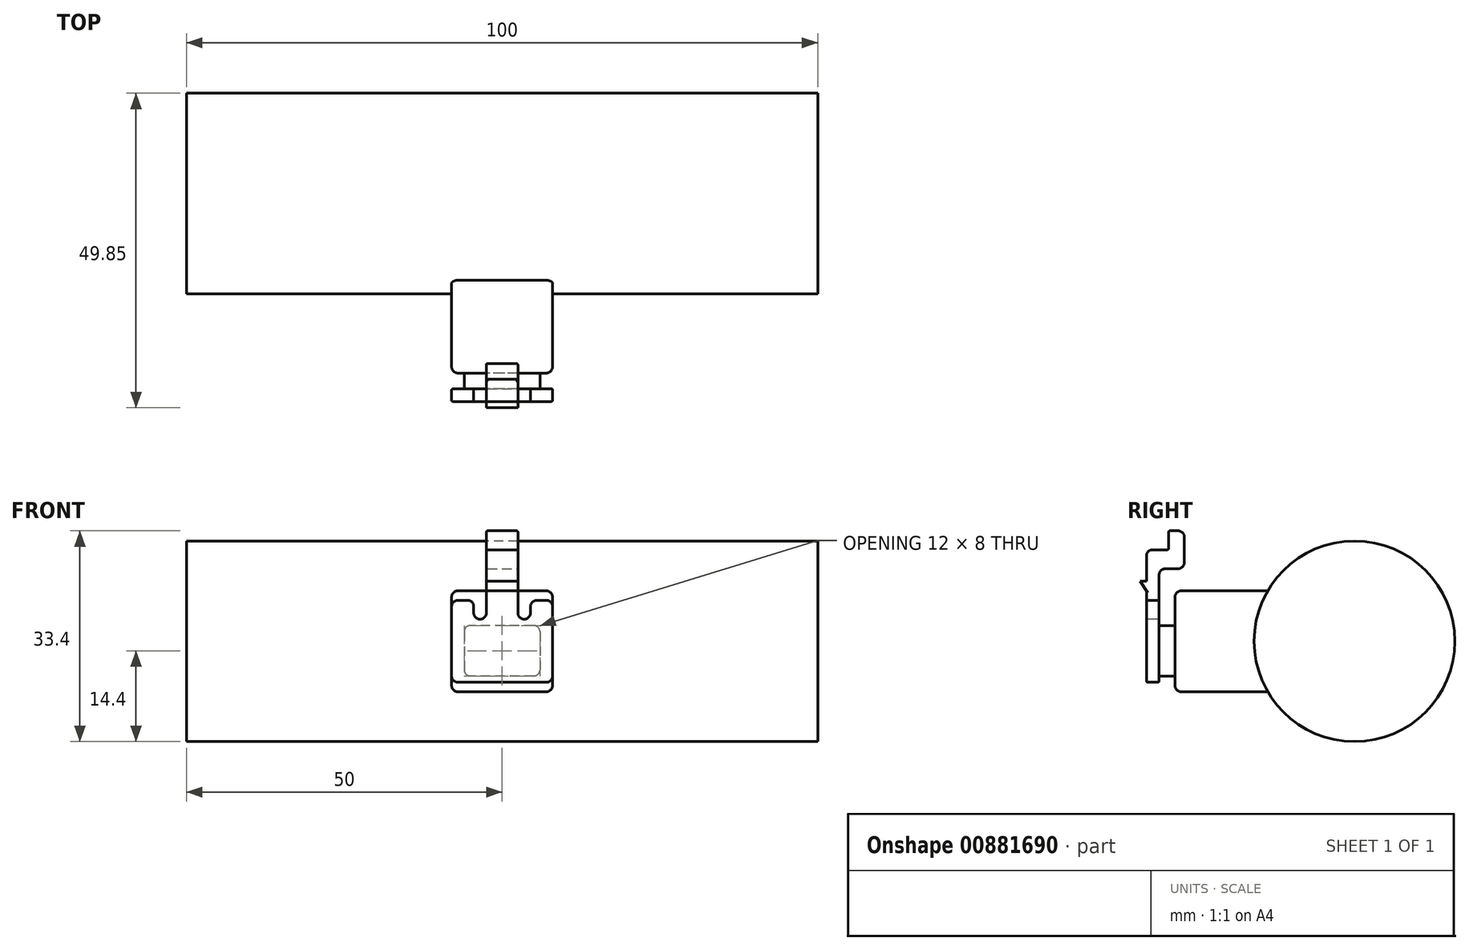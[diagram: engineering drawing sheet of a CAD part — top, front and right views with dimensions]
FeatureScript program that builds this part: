
annotation { "Feature Type Name" : "Feature", "Feature Type Description" : "" }
export const myFeature = defineFeature(function(context is Context, id is Id, definition is map)
    precondition{}
    {
        {
            var Q0;
            Q0=qCreatedBy(makeId("Front.planeOp"),FACE);
            var sketch = newSketch(context, id + "F0", { "sketchPlane" : qUnion([Q0])});
            skLineSegment(sketch, "E0.bottom", {"start": v(8, -5) * mm, "end": v(-8, -5) * mm});
            skLineSegment(sketch, "E0.top", {"start": v(8, 5) * mm, "end": v(-8, 5) * mm});
            skLineSegment(sketch, "E0.left", {"start": v(8, -5) * mm, "end": v(8, 5) * mm});
            skLineSegment(sketch, "E0.right", {"start": v(-8, -5) * mm, "end": v(-8, 5) * mm});
            skPoint(sketch, "E0.middle", {"position": v(0, 0) * mm});
            skPoint(sketch, "E1", {"position": v(0, 5) * mm});
            skLineSegment(sketch, "E2.bottom", {"start": v(-2.5, 13) * mm, "end": v(2.5, 13) * mm});
            skLineSegment(sketch, "E2.top", {"start": v(-2.5, 5) * mm, "end": v(2.5, 5) * mm});
            skLineSegment(sketch, "E2.left", {"start": v(-2.5, 13) * mm, "end": v(-2.5, 5) * mm});
            skLineSegment(sketch, "E2.right", {"start": v(2.5, 13) * mm, "end": v(2.5, 5) * mm});
            skLineSegment(sketch, "E3.bottom", {"start": v(-8, 8) * mm, "end": v(-4.5, 8) * mm});
            skLineSegment(sketch, "E3.top", {"start": v(-8, 5) * mm, "end": v(-4.5, 5) * mm});
            skLineSegment(sketch, "E3.left", {"start": v(-8, 8) * mm, "end": v(-8, 5) * mm});
            skLineSegment(sketch, "E3.right", {"start": v(-4.5, 8) * mm, "end": v(-4.5, 5) * mm});
            skLineSegment(sketch, "E4.bottom", {"start": v(4.5, 8) * mm, "end": v(8, 8) * mm});
            skLineSegment(sketch, "E4.top", {"start": v(4.5, 5) * mm, "end": v(8, 5) * mm});
            skLineSegment(sketch, "E4.left", {"start": v(4.5, 8) * mm, "end": v(4.5, 5) * mm});
            skLineSegment(sketch, "E4.right", {"start": v(8, 8) * mm, "end": v(8, 5) * mm});
            skLineSegment(sketch, "E5.top", {"start": v(-2.5, 16) * mm, "end": v(2.5, 16) * mm});
            skLineSegment(sketch, "E5.left", {"start": v(-2.5, 13) * mm, "end": v(-2.5, 16) * mm});
            skLineSegment(sketch, "E5.right", {"start": v(2.5, 13) * mm, "end": v(2.5, 16) * mm});
            skPoint(sketch, "E6.visualSharp", {"position": v(-8, -5) * mm});
            skLineSegment(sketch, "E6.filletArc", {"start": v(-8, -5) * mm, "end": v(-8, -5) * mm});
            skPoint(sketch, "E7.visualSharp", {"position": v(8, -5) * mm});
            skLineSegment(sketch, "E7.filletArc", {"start": v(8, -5) * mm, "end": v(8, -5) * mm});
            skPoint(sketch, "E8.visualSharp", {"position": v(8, 8) * mm});
            skLineSegment(sketch, "E8.filletArc", {"start": v(8, 8) * mm, "end": v(8, 8) * mm});
            skPoint(sketch, "E9.visualSharp", {"position": v(4.5, 8) * mm});
            skLineSegment(sketch, "E9.filletArc", {"start": v(4.5, 8) * mm, "end": v(4.5, 8) * mm});
            skPoint(sketch, "E10.visualSharp", {"position": v(-4.5, 8) * mm});
            skLineSegment(sketch, "E10.filletArc", {"start": v(-4.5, 8) * mm, "end": v(-4.5, 8) * mm});
            skPoint(sketch, "E11.visualSharp", {"position": v(-8, 8) * mm});
            skLineSegment(sketch, "E11.filletArc", {"start": v(-8, 8) * mm, "end": v(-8, 8) * mm});
            skLineSegment(sketch, "E12.bottom", {"start": v(2.5, 11) * mm, "end": v(-2.5, 11) * mm});
            skLineSegment(sketch, "E12.top", {"start": v(2.5, 9.5) * mm, "end": v(-2.5, 9.5) * mm});
            skLineSegment(sketch, "E12.left", {"start": v(2.5, 11) * mm, "end": v(2.5, 9.5) * mm});
            skLineSegment(sketch, "E12.right", {"start": v(-2.5, 11) * mm, "end": v(-2.5, 9.5) * mm});
            skPoint(sketch, "E13", {"position": v(0, 9.5) * mm});
            skSolve(sketch);
        }
        {
            var Q0;
            {var subQ0=sQuery(id+"F0.wireOp",EDGE,"E2.bottom");var subQ1=makeQuery(id+"F0.imprint","IMPRINT",EDGE,{"derivedFrom":subQ0});var subQ4=sQuery(id+"F0.wireOp",EDGE,"E12.top");var subQ7=sQuery(id+"F0.wireOp",EDGE,"E12.bottom");var subQ12=makeQuery(id+"F0.imprint","IMPRINT",EDGE,{"derivedFrom":subQ7});var subQ13=makeQuery(id+"F0.imprint","IMPRINT",EDGE,{"derivedFrom":subQ4});Q0=qUnion([makeQuery(id+"F0.imprint","IMPRINT",FACE,{"disambiguationData":[TD([[subQ13,1.0]])]}),makeQuery(id+"F0.imprint","IMPRINT",FACE,{"disambiguationData":[TD([[makeQuery(id+"F0.imprint","IMPRINT",EDGE,{"derivedFrom":sQuery(id+"F0.wireOp",EDGE,"E0.bottom")}),-1.0]])]}),makeQuery(id+"F0.imprint","IMPRINT",FACE,{"disambiguationData":[TD([[makeQuery(id+"F0.imprint","IMPRINT",EDGE,{"derivedFrom":sQuery(id+"F0.wireOp",EDGE,"E4.bottom")}),-1.0]])]}),makeQuery(id+"F0.imprint","IMPRINT",FACE,{"disambiguationData":[TD([[subQ1,-1.0]])]}),makeQuery(id+"F0.imprint","IMPRINT",FACE,{"disambiguationData":[TD([[makeQuery(id+"F0.imprint","IMPRINT",EDGE,{"derivedFrom":sQuery(id+"F0.wireOp",EDGE,"E3.bottom")}),-1.0]])]}),makeQuery(id+"F0.imprint","IMPRINT",FACE,{"disambiguationData":[TD([[subQ12,1.0]])]}),makeQuery(id+"F0.imprint","IMPRINT",FACE,{"disambiguationData":[TD([[subQ1,1.0]])]})]);}
            extrude(context, id + "F1", {"entities" : qUnion([Q0]), "oppositeDirection" : true, "depth" : 2 * mm, "offsetDistance" : 25 * mm});
        }
        {
            var Q0;
            Q0=makeQuery(id+"F0.imprint","IMPRINT",FACE,{"disambiguationData":[TD([[makeQuery(id+"F0.imprint","IMPRINT",EDGE,{"derivedFrom":sQuery(id+"F0.wireOp",EDGE,"E2.bottom")}),1.0]])]});
            extrude(context, id + "F2", {"entities" : qUnion([Q0]), "operationType" : NewBodyOperationType.ADD, "oppositeDirection" : true, "depth" : 6 * mm, "offsetDistance" : 25 * mm, "hasSecondDirection" : true, "secondDirectionOppositeDirection" : true, "secondDirectionDepth" : 2 * mm});
        }
        {
            var Q0;
            {var subQ0=sQuery(id+"F0.wireOp",EDGE,"E5.top");Q0=makeQuery(id+"F2.boolean.opBoolean","MERGE",FACE,{"derivedFrom":[makeQuery(id+"F1.opExtrude","SWEPT_FACE",FACE,{"disambiguationData":[OSD([subQ0])]}),makeQuery(id+"F2.opExtrude","SWEPT_FACE",FACE,{"disambiguationData":[OSD([subQ0])]})]});}
            cPlane(context, id + "F3", {"entities" : qUnion([Q0]), "cplaneType" : CPlaneType.OFFSET, "offset" : 0 * mm, "width" : 150 * mm, "height" : 150 * mm});
        }
        {
            var Q0;
            Q0=qCreatedBy(id+"F3.planeOp",FACE);
            var sketch = newSketch(context, id + "F4", { "sketchPlane" : qUnion([Q0])});
            skPoint(sketch, "E14.0", {"position": v(2.5, 6) * mm});
            skPoint(sketch, "E15.0", {"position": v(-2.5, 6) * mm});
            skLineSegment(sketch, "E16.bottom", {"start": v(-2.5, 6) * mm, "end": v(2.5, 6) * mm});
            skLineSegment(sketch, "E16.top", {"start": v(-2.5, 3.5) * mm, "end": v(2.5, 3.5) * mm});
            skLineSegment(sketch, "E16.left", {"start": v(2.5, 6) * mm, "end": v(2.5, 3.5) * mm});
            skLineSegment(sketch, "E16.right", {"start": v(-2.5, 6) * mm, "end": v(-2.5, 3.5) * mm});
            skSolve(sketch);
        }
        {
            var Q0;
            Q0 = qSketchRegion(id + "F4", true);
            extrude(context, id + "F5", {"entities" : qUnion([Q0]), "operationType" : NewBodyOperationType.ADD, "depth" : 3 * mm, "offsetDistance" : 25 * mm});
        }
        {
            var Q0;
            {var subQ2=sQuery(id+"F0.wireOp",EDGE,"E12.bottom");Q0=makeQuery(id+"F0.imprint","IMPRINT",FACE,{"disambiguationData":[TD([[makeQuery(id+"F0.imprint","IMPRINT",EDGE,{"derivedFrom":subQ2}),1.0]])]});}
            extrude(context, id + "F6", {"entities" : qUnion([Q0]), "operationType" : NewBodyOperationType.ADD, "depth" : 1 * mm, "offsetDistance" : 25 * mm});
        }
        {
            var Q0;
            Q0=makeQuery(id+"F6.opExtrude","CAP_EDGE",EDGE,{"disambiguationData":[OSD([sQuery(id+"F0.wireOp",EDGE,"E12.top")])],"isStart":false});
            chamfer(context, id + "F7", {"entities" : qUnion([Q0]), "chamferType" : ChamferType.TWO_OFFSETS, "width1" : 1 * mm, "oppositeDirection" : false, "width2" : 1.5 * mm});
        }
        {
            var Q0;
            Q0=makeQuery(id+"F1.opExtrude","CAP_FACE",FACE,{"disambiguationData":[OSD([sQuery(id+"F0.wireOp",EDGE,"E0.bottom"),sQuery(id+"F0.wireOp",EDGE,"E0.top"),sQuery(id+"F0.wireOp",EDGE,"E0.left"),sQuery(id+"F0.wireOp",EDGE,"E0.right"),sQuery(id+"F0.wireOp",EDGE,"E2.left"),sQuery(id+"F0.wireOp",EDGE,"E2.right"),sQuery(id+"F0.wireOp",EDGE,"E3.bottom"),sQuery(id+"F0.wireOp",EDGE,"E3.left"),sQuery(id+"F0.wireOp",EDGE,"E3.right"),sQuery(id+"F0.wireOp",EDGE,"E4.bottom"),sQuery(id+"F0.wireOp",EDGE,"E4.left"),sQuery(id+"F0.wireOp",EDGE,"E4.right"),sQuery(id+"F0.wireOp",EDGE,"E5.top"),sQuery(id+"F0.wireOp",EDGE,"E5.left"),sQuery(id+"F0.wireOp",EDGE,"E5.right")])],"isStart":false});
            cPlane(context, id + "F8", {"entities" : qUnion([Q0]), "cplaneType" : CPlaneType.OFFSET, "offset" : 0 * mm, "width" : 150 * mm, "height" : 150 * mm});
        }
        {
            var Q0;
            Q0=qCreatedBy(id+"F8.planeOp",FACE);
            var sketch = newSketch(context, id + "F9", { "sketchPlane" : qUnion([Q0])});
            skLineSegment(sketch, "E17.bottom", {"start": v(-6, 4) * mm, "end": v(6, 4) * mm});
            skLineSegment(sketch, "E17.top", {"start": v(-6, -4) * mm, "end": v(6, -4) * mm});
            skLineSegment(sketch, "E17.left", {"start": v(-6, 4) * mm, "end": v(-6, -4) * mm});
            skLineSegment(sketch, "E17.right", {"start": v(6, 4) * mm, "end": v(6, -4) * mm});
            skPoint(sketch, "E18.0", {"position": v(8, 5) * mm});
            skPoint(sketch, "E19.0", {"position": v(-8, 5) * mm});
            skPoint(sketch, "E20.0", {"position": v(0, 5) * mm});
            skPoint(sketch, "E21", {"position": v(0, 4) * mm});
            skPoint(sketch, "E22.visualSharp", {"position": v(-6, 4) * mm});
            skLineSegment(sketch, "E22.filletArc", {"start": v(-6, 4) * mm, "end": v(-6, 4) * mm});
            skPoint(sketch, "E23.visualSharp", {"position": v(-6, -4) * mm});
            skLineSegment(sketch, "E23.filletArc", {"start": v(-6, -4) * mm, "end": v(-6, -4) * mm});
            skPoint(sketch, "E24.visualSharp", {"position": v(6, -4) * mm});
            skLineSegment(sketch, "E24.filletArc", {"start": v(6, -4) * mm, "end": v(6, -4) * mm});
            skPoint(sketch, "E25.visualSharp", {"position": v(6, 4) * mm});
            skLineSegment(sketch, "E25.filletArc", {"start": v(6, 4) * mm, "end": v(6, 4) * mm});
            skSolve(sketch);
        }
        {
            var Q0;
            Q0=makeQuery(id+"F9.imprint","IMPRINT",FACE,{"disambiguationData":[TD([[makeQuery(id+"F9.imprint","IMPRINT",EDGE,{"derivedFrom":sQuery(id+"F9.wireOp",EDGE,"E17.bottom")}),-1.0]])]});
            extrude(context, id + "F10", {"entities" : qUnion([Q0]), "operationType" : NewBodyOperationType.ADD, "depth" : 2.5 * mm, "offsetDistance" : 25 * mm});
        }
        {
            var Q0;
            Q0=makeQuery(id+"F10.opExtrude","CAP_FACE",FACE,{"disambiguationData":[OSD([sQuery(id+"F9.wireOp",EDGE,"E17.bottom"),sQuery(id+"F9.wireOp",EDGE,"E17.top"),sQuery(id+"F9.wireOp",EDGE,"E17.left"),sQuery(id+"F9.wireOp",EDGE,"E17.right")])],"isStart":false});
            cPlane(context, id + "F11", {"entities" : qUnion([Q0]), "cplaneType" : CPlaneType.OFFSET, "offset" : 0 * mm, "width" : 150 * mm, "height" : 150 * mm});
        }
        {
            var Q0;
            Q0=qCreatedBy(id+"F11.planeOp",FACE);
            var sketch = newSketch(context, id + "F12", { "sketchPlane" : qUnion([Q0])});
            skLineSegment(sketch, "E26.bottom", {"start": v(-8, 9.5) * mm, "end": v(8, 9.5) * mm});
            skLineSegment(sketch, "E26.top", {"start": v(-8, -6.5) * mm, "end": v(8, -6.5) * mm});
            skLineSegment(sketch, "E26.left", {"start": v(-8, 9.5) * mm, "end": v(-8, -6.5) * mm});
            skLineSegment(sketch, "E26.right", {"start": v(8, 9.5) * mm, "end": v(8, -6.5) * mm});
            skPoint(sketch, "E27", {"position": v(0, 9.5) * mm});
            skPoint(sketch, "E28", {"position": v(8, 1.5) * mm});
            skSolve(sketch);
        }
        {
            var Q0;
            Q0=makeQuery(id+"F12.imprint","IMPRINT",FACE,{"disambiguationData":[TD([[makeQuery(id+"F12.imprint","IMPRINT",EDGE,{"derivedFrom":sQuery(id+"F12.wireOp",EDGE,"E26.bottom")}),-1.0]])]});
            extrude(context, id + "F13", {"entities" : qUnion([Q0]), "operationType" : NewBodyOperationType.ADD, "depth" : 15 * mm, "offsetDistance" : 25 * mm});
        }
        {
            var Q0;
            Q0=qCreatedBy(makeId("Right.planeOp"),FACE);
            var sketch = newSketch(context, id + "F14", { "sketchPlane" : qUnion([Q0])});
            skCircle(sketch, "E29", {"center": v(32.95, 1.5) * mm, "radius": 15.9 * mm});
            skSolve(sketch);
        }
        {
            var Q0;
            Q0=makeQuery(id+"F14.imprint","IMPRINT",FACE,{"disambiguationData":[TD([[makeQuery(id+"F14.imprint","IMPRINT",EDGE,{"derivedFrom":sQuery(id+"F14.wireOp",EDGE,"E29")}),1.0]])]});
            extrude(context, id + "F15", {"entities" : qUnion([Q0]), "operationType" : NewBodyOperationType.REMOVE, "endBound" : BoundingType.SYMMETRIC, "depth" : 80 * mm, "offsetDistance" : 25 * mm});
        }
        {
            var Q0;
            Q0=makeQuery(id+"F2.boolean.opBoolean","INTERSECT",EDGE,{"derivedFrom":[makeQuery(id+"F1.opExtrude","CAP_FACE",FACE,{"disambiguationData":[OSD([sQuery(id+"F0.wireOp",EDGE,"E0.bottom"),sQuery(id+"F0.wireOp",EDGE,"E0.top"),sQuery(id+"F0.wireOp",EDGE,"E0.left"),sQuery(id+"F0.wireOp",EDGE,"E0.right"),sQuery(id+"F0.wireOp",EDGE,"E2.left"),sQuery(id+"F0.wireOp",EDGE,"E2.right"),sQuery(id+"F0.wireOp",EDGE,"E3.bottom"),sQuery(id+"F0.wireOp",EDGE,"E3.left"),sQuery(id+"F0.wireOp",EDGE,"E3.right"),sQuery(id+"F0.wireOp",EDGE,"E4.bottom"),sQuery(id+"F0.wireOp",EDGE,"E4.left"),sQuery(id+"F0.wireOp",EDGE,"E4.right"),sQuery(id+"F0.wireOp",EDGE,"E5.top"),sQuery(id+"F0.wireOp",EDGE,"E5.left"),sQuery(id+"F0.wireOp",EDGE,"E5.right"),sQuery(id+"F0.wireOp",EDGE,"E6.filletArc"),sQuery(id+"F0.wireOp",EDGE,"E7.filletArc"),sQuery(id+"F0.wireOp",EDGE,"E8.filletArc"),sQuery(id+"F0.wireOp",EDGE,"E9.filletArc"),sQuery(id+"F0.wireOp",EDGE,"E10.filletArc"),sQuery(id+"F0.wireOp",EDGE,"E11.filletArc")])],"isStart":false}),makeQuery(id+"F2.opExtrude","SWEPT_FACE",FACE,{"disambiguationData":[OSD([sQuery(id+"F0.wireOp",EDGE,"E2.bottom")])]})]});
            var Q1;
            Q1=makeQuery(id+"F2.opExtrude","CAP_EDGE",EDGE,{"disambiguationData":[OSD([sQuery(id+"F0.wireOp",EDGE,"E2.bottom")])],"isStart":false});
            var Q2;
            Q2=makeQuery(id+"F1.opExtrude","CAP_EDGE",EDGE,{"disambiguationData":[OSD([sQuery(id+"F0.wireOp",EDGE,"E5.top")])],"isStart":true});
            var Q3;
            Q3=makeQuery(id+"F5.opExtrude","CAP_EDGE",EDGE,{"disambiguationData":[OSD([sQuery(id+"F4.wireOp",EDGE,"E16.top")])],"isStart":true});
            var Q4;
            Q4=makeQuery(id+"F1.opExtrude","SWEPT_EDGE",EDGE,{"disambiguationData":[OSD([sQuery(id+"F0.wireOp",EDGE,"E0.top"),sQuery(id+"F0.wireOp",EDGE,"E2.left")])]});
            var Q5;
            Q5=makeQuery(id+"F1.opExtrude","SWEPT_EDGE",EDGE,{"disambiguationData":[OSD([sQuery(id+"F0.wireOp",EDGE,"E0.top"),sQuery(id+"F0.wireOp",EDGE,"E2.right")])]});
            var Q6;
            Q6=makeQuery(id+"F5.opExtrude","CAP_EDGE",EDGE,{"disambiguationData":[OSD([sQuery(id+"F4.wireOp",EDGE,"E16.bottom")])],"isStart":false});
            var Q7;
            Q7=makeQuery(id+"F10.opExtrude","SWEPT_EDGE",EDGE,{"disambiguationData":[OSD([sQuery(id+"F9.wireOp",EDGE,"E17.top"),sQuery(id+"F9.wireOp",EDGE,"E17.left")])]});
            var Q8;
            Q8=makeQuery(id+"F1.opExtrude","SWEPT_EDGE",EDGE,{"disambiguationData":[OSD([sQuery(id+"F0.wireOp",EDGE,"E0.bottom"),sQuery(id+"F0.wireOp",EDGE,"E0.right")])]});
            var Q9;
            Q9=makeQuery(id+"F1.opExtrude","SWEPT_EDGE",EDGE,{"disambiguationData":[OSD([sQuery(id+"F0.wireOp",EDGE,"E0.bottom"),sQuery(id+"F0.wireOp",EDGE,"E0.left")])]});
            var Q10;
            Q10=makeQuery(id+"F1.opExtrude","SWEPT_EDGE",EDGE,{"disambiguationData":[OSD([sQuery(id+"F0.wireOp",EDGE,"E4.bottom"),sQuery(id+"F0.wireOp",EDGE,"E4.right")])]});
            var Q11;
            Q11=makeQuery(id+"F1.opExtrude","SWEPT_EDGE",EDGE,{"disambiguationData":[OSD([sQuery(id+"F0.wireOp",EDGE,"E4.bottom"),sQuery(id+"F0.wireOp",EDGE,"E4.left")])]});
            var Q12;
            Q12=makeQuery(id+"F1.opExtrude","SWEPT_EDGE",EDGE,{"disambiguationData":[OSD([sQuery(id+"F0.wireOp",EDGE,"E3.bottom"),sQuery(id+"F0.wireOp",EDGE,"E3.right")])]});
            var Q13;
            Q13=makeQuery(id+"F1.opExtrude","SWEPT_EDGE",EDGE,{"disambiguationData":[OSD([sQuery(id+"F0.wireOp",EDGE,"E3.bottom"),sQuery(id+"F0.wireOp",EDGE,"E3.left")])]});
            var Q14;
            Q14=makeQuery(id+"F10.opExtrude","SWEPT_EDGE",EDGE,{"disambiguationData":[OSD([sQuery(id+"F9.wireOp",EDGE,"E17.top"),sQuery(id+"F9.wireOp",EDGE,"E17.right")])]});
            var Q15;
            Q15=makeQuery(id+"F10.opExtrude","SWEPT_EDGE",EDGE,{"disambiguationData":[OSD([sQuery(id+"F9.wireOp",EDGE,"E17.bottom"),sQuery(id+"F9.wireOp",EDGE,"E17.right")])]});
            var Q16;
            Q16=makeQuery(id+"F10.opExtrude","SWEPT_EDGE",EDGE,{"disambiguationData":[OSD([sQuery(id+"F9.wireOp",EDGE,"E17.bottom"),sQuery(id+"F9.wireOp",EDGE,"E17.left")])]});
            var Q17;
            Q17=makeQuery(id+"F1.opExtrude","SWEPT_EDGE",EDGE,{"disambiguationData":[OSD([sQuery(id+"F0.wireOp",EDGE,"E0.top"),sQuery(id+"F0.wireOp",EDGE,"E3.right")])]});
            var Q18;
            Q18=makeQuery(id+"F1.opExtrude","SWEPT_EDGE",EDGE,{"disambiguationData":[OSD([sQuery(id+"F0.wireOp",EDGE,"E0.top"),sQuery(id+"F0.wireOp",EDGE,"E4.left")])]});
            var Q19;
            Q19=makeQuery(id+"F13.opExtrude","CAP_EDGE",EDGE,{"disambiguationData":[OSD([sQuery(id+"F12.wireOp",EDGE,"E26.right")])],"isStart":true});
            var Q20;
            Q20=makeQuery(id+"F13.opExtrude","CAP_EDGE",EDGE,{"disambiguationData":[OSD([sQuery(id+"F12.wireOp",EDGE,"E26.bottom")])],"isStart":true});
            var Q21;
            Q21=makeQuery(id+"F13.opExtrude","CAP_EDGE",EDGE,{"disambiguationData":[OSD([sQuery(id+"F12.wireOp",EDGE,"E26.top")])],"isStart":true});
            var Q22;
            Q22=makeQuery(id+"F13.opExtrude","CAP_EDGE",EDGE,{"disambiguationData":[OSD([sQuery(id+"F12.wireOp",EDGE,"E26.left")])],"isStart":true});
            var Q23;
            Q23=makeQuery(id+"F13.opExtrude","SWEPT_EDGE",EDGE,{"disambiguationData":[OSD([sQuery(id+"F12.wireOp",EDGE,"E26.top"),sQuery(id+"F12.wireOp",EDGE,"E26.left")])]});
            var Q24;
            Q24=makeQuery(id+"F13.opExtrude","SWEPT_EDGE",EDGE,{"disambiguationData":[OSD([sQuery(id+"F12.wireOp",EDGE,"E26.bottom"),sQuery(id+"F12.wireOp",EDGE,"E26.left")])]});
            var Q25;
            Q25=makeQuery(id+"F13.opExtrude","SWEPT_EDGE",EDGE,{"disambiguationData":[OSD([sQuery(id+"F12.wireOp",EDGE,"E26.bottom"),sQuery(id+"F12.wireOp",EDGE,"E26.right")])]});
            var Q26;
            Q26=makeQuery(id+"F13.opExtrude","SWEPT_EDGE",EDGE,{"disambiguationData":[OSD([sQuery(id+"F12.wireOp",EDGE,"E26.top"),sQuery(id+"F12.wireOp",EDGE,"E26.right")])]});
            fillet(context, id + "F16", {"entities" : qUnion([Q0, Q1, Q2, Q3, Q4, Q5, Q6, Q7, Q8, Q9, Q10, Q11, Q12, Q13, Q14, Q15, Q16, Q17, Q18, Q19, Q20, Q21, Q22, Q23, Q24, Q25, Q26]), "radius" : 1 * mm, "tangentPropagation" : true, "allowEdgeOverflow" : false});
        }
        {
            var Q0;
            Q0=makeQuery(id+"F5.opExtrude","SWEPT_EDGE",EDGE,{"disambiguationData":[OSD([sQuery(id+"F4.wireOp",EDGE,"E16.top"),sQuery(id+"F4.wireOp",EDGE,"E16.left")])]});
            var Q1;
            Q1=makeQuery(id+"F5.opExtrude","SWEPT_FACE",FACE,{"disambiguationData":[OSD([sQuery(id+"F4.wireOp",EDGE,"E16.top")])]});
            var Q2;
            Q2=makeQuery(id+"F5.opExtrude","CAP_EDGE",EDGE,{"disambiguationData":[OSD([sQuery(id+"F4.wireOp",EDGE,"E16.left")])],"isStart":false});
            var Q3;
            {var subQ0=sQuery(id+"F0.wireOp",EDGE,"E2.right");var subQ1=sQuery(id+"F0.wireOp",EDGE,"E5.right");Q3=makeQuery(id+"F16.opFillet","BLEND_EDGE",EDGE,{"blendedFrom":[makeQuery(id+"F5.opExtrude","CAP_EDGE",EDGE,{"disambiguationData":[OSD([sQuery(id+"F4.wireOp",EDGE,"E16.bottom")])],"isStart":false}),makeQuery(id+"F6.boolean.opBoolean","MERGE",FACE,{"derivedFrom":[makeQuery(id+"F5.boolean.opBoolean","MERGE",FACE,{"derivedFrom":[makeQuery(id+"F2.boolean.opBoolean","MERGE",FACE,{"derivedFrom":[makeQuery(id+"F1.opExtrude","SWEPT_FACE",FACE,{"disambiguationData":[OSD([subQ0,subQ1])]}),makeQuery(id+"F2.opExtrude","SWEPT_FACE",FACE,{"disambiguationData":[OSD([subQ1])]})]}),makeQuery(id+"F5.opExtrude","SWEPT_FACE",FACE,{"disambiguationData":[OSD([sQuery(id+"F4.wireOp",EDGE,"E16.left")])]})]}),makeQuery(id+"F6.opExtrude","SWEPT_FACE",FACE,{"disambiguationData":[OSD([subQ0])]})]})],"blendedInto":[makeQuery(id+"F6.boolean.opBoolean","MERGE",FACE,{"derivedFrom":[makeQuery(id+"F5.boolean.opBoolean","MERGE",FACE,{"derivedFrom":[makeQuery(id+"F2.boolean.opBoolean","MERGE",FACE,{"derivedFrom":[makeQuery(id+"F1.opExtrude","SWEPT_FACE",FACE,{"disambiguationData":[OSD([subQ0,subQ1])]}),makeQuery(id+"F2.opExtrude","SWEPT_FACE",FACE,{"disambiguationData":[OSD([subQ1])]})]}),makeQuery(id+"F5.opExtrude","SWEPT_FACE",FACE,{"disambiguationData":[OSD([sQuery(id+"F4.wireOp",EDGE,"E16.left")])]})]}),makeQuery(id+"F6.opExtrude","SWEPT_FACE",FACE,{"disambiguationData":[OSD([subQ0])]})]})]});}
            var Q4;
            Q4=makeQuery(id+"F1.opExtrude","CAP_EDGE",EDGE,{"disambiguationData":[OSD([sQuery(id+"F0.wireOp",EDGE,"E3.bottom")])],"isStart":true});
            var Q5;
            Q5=makeQuery(id+"F10.opExtrude","CAP_EDGE",EDGE,{"disambiguationData":[OSD([sQuery(id+"F9.wireOp",EDGE,"E17.right")])],"isStart":false});
            var Q6;
            Q6=makeQuery(id+"F10.opExtrude","CAP_EDGE",EDGE,{"disambiguationData":[OSD([sQuery(id+"F9.wireOp",EDGE,"E17.top")])],"isStart":true});
            fillet(context, id + "F17", {"entities" : qUnion([Q0, Q1, Q2, Q3, Q4, Q5, Q6]), "radius" : 0.2 * mm, "tangentPropagation" : true, "allowEdgeOverflow" : false});
        }
        {
            var Q0;
            Q0=makeQuery(id+"F14.imprint","IMPRINT",FACE,{"disambiguationData":[TD([[makeQuery(id+"F14.imprint","IMPRINT",EDGE,{"derivedFrom":sQuery(id+"F14.wireOp",EDGE,"E29")}),1.0]])]});
            extrude(context, id + "F18", {"entities" : qUnion([Q0]), "operationType" : NewBodyOperationType.ADD, "endBound" : BoundingType.SYMMETRIC, "depth" : 100 * mm, "offsetDistance" : 25 * mm});
        }
    });
